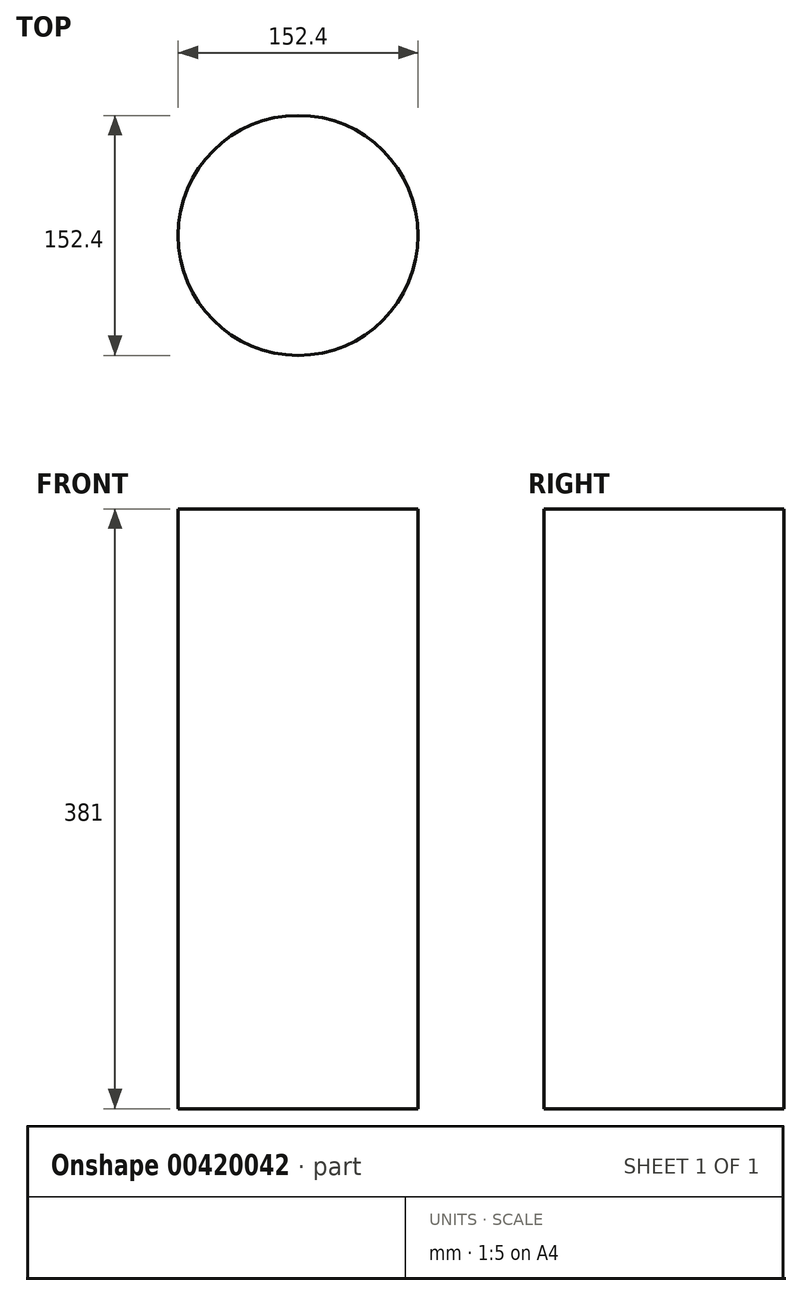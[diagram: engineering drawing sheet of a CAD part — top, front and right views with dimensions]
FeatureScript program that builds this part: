
annotation { "Feature Type Name" : "Feature", "Feature Type Description" : "" }
export const myFeature = defineFeature(function(context is Context, id is Id, definition is map)
    precondition{}
    {
        {
            var Q0;
            Q0=qCreatedBy(makeId("Top.planeOp"),FACE);
            var sketch = newSketch(context, id + "F0", { "sketchPlane" : qUnion([Q0])});
            skCircle(sketch, "E0", {"center": v(0, 0) * mm, "radius": 76.2 * mm});
            skSolve(sketch);
        }
        {
            var Q0;
            Q0=makeQuery(id+"F0.imprint","IMPRINT",FACE,{"disambiguationData":[TD([[makeQuery(id+"F0.imprint","IMPRINT",EDGE,{"derivedFrom":sQuery(id+"F0.wireOp",EDGE,"E0")}),1.0]])]});
            extrude(context, id + "F1", {"entities" : qUnion([Q0]), "depth" : 381 * mm});
        }
    });
